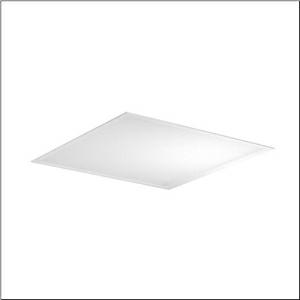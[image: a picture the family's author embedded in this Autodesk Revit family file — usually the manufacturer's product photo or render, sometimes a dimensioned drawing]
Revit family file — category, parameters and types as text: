
# Revit family: apollon_21_square_51mq12wc2454
name_source: partatom
category: Lighting Fixtures
units: mm (PartAtom-declared; Revit-internal decimal feet)

## family parameters
Cut with Voids When Loaded = No
Host = Face
Light Source = No
Part Type = Normal
Room Calculation Point = No
Round Connector Dimension = Use Diameter
Shared = No

## types (1)
- Apollon 21 square (1 x LED, 4200 lm, 24.7 W, 4000K)
    Apparent Load = 25 VA
    CIE Flux Codes = 60 87 97 100 100
    Color Rendering = 80
    Color Temperature = 4000K
    Default Elevation = 1800 mm
    Description = Apollon 21 square, office luminaire, primary optical cover: micro prismatic cover, of PMMA, CAT 2 (L<= 3000cd/m²), light emission: direct distribution, primary light characteristic: symmetric, installation type: lay-in mounting, LED, rated luminous flux: 4.200lm, luminous efficacy: 170lm/W, light colour: 840, colour temperature: 4000K, control gear: DALI 2, Multilumen, with terminal, 5-pole, mains connection: 220..240V, AC/DC, 0/50..60Hz, rated input power: 24.7W, housing, of aluminium, coated, traffic white (RAL 9016), module: M600, length: 595mm, width: 595mm, height: 55mm, recess depth: 180mm, housing upper side, of sheet steel, galvanised, protection rating (complete): IP20, protection rating (lamp compartment, on room side): IP54, insulation class (complete): insulation class II (safety insulation), certification: CE, ENEC, impact resistance: IK03, permissible operating ambient temperature: -20..+45°C, permissible storage temperature: -40..+80°C, standard: EN 60598-2-22, packaging unit: 1 piece
    Height = 0 mm  [stored 0 ft]
    Lamp = 1 x LED
    Lamp Light Flux = 4200 lm
    Lamp Power = 24.7 W
    Lamp count = 1
    Length = 595 mm
    Luminous efficacy = 170 lm/W
    Manufacturer = Siteco
    ModVariant = No
    Model = 51MQ12WC2454
    Mounting Place = Ceiling
    Mounting Type = Recessed
    Number of Poles = 1
    OnlyDefault = Yes
    Power Factor = 1
    Product Name = Apollon 21 square
    Product group = office luminaire | ceiling recessed
    ProductGroupID = 401
    Protection Class = Protection class II
    Protection Degree = IP 20
    RLX_Detail_Level = 1
    RLX_Emergency_Light_Flux = 0 lm
    RLX_Emergency_Type = 0
    RLX_Emergency_Type_DB = No
    RlxData = <blob elided: 12561 chars, md5=44365f1c>
    Socket = socket
    Standby Power = 0 W
    System Light Flux = 4200 lm
    System Power = 25 W
    Type Comments = Product without accessories
    Type Image = l_1291049.jpg
    URL = http://relux.com
    VarID = ---
    Voltage = 0 V
    Weight = 0.00 kg
    Width = 595 mm

note: [stored X ft] marks values corroborated as IEEE doubles in the binary element streams (Revit-internal decimal feet)

## geometry (parser evidence)
native form markers: Sweep x9
no freeform markers — native parametric forms only
